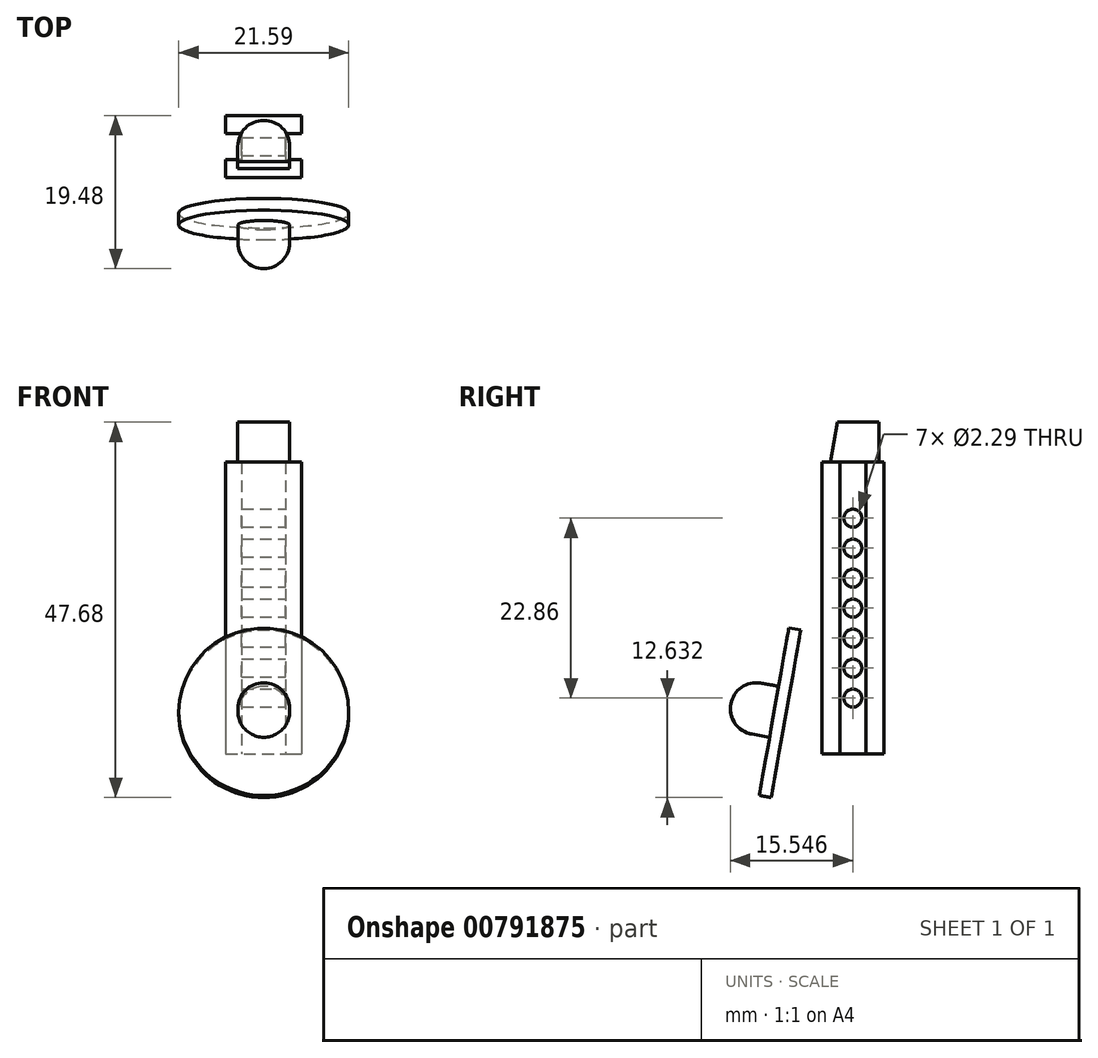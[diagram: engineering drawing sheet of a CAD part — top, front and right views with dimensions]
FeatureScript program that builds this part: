
annotation { "Feature Type Name" : "Feature", "Feature Type Description" : "" }
export const myFeature = defineFeature(function(context is Context, id is Id, definition is map)
    precondition{}
    {
        {
            var Q0;
            Q0=qCreatedBy(makeId("Top.planeOp"),FACE);
            var sketch = newSketch(context, id + "F0", { "sketchPlane" : qUnion([Q0])});
            skLineSegment(sketch, "E0.bottom", {"start": v(3.45, -0.54) * mm, "end": v(13.1, -0.54) * mm});
            skLineSegment(sketch, "E0.top", {"start": v(3.45, -8.41) * mm, "end": v(13.1, -8.41) * mm});
            skLineSegment(sketch, "E0.left", {"start": v(3.45, -0.54) * mm, "end": v(3.45, -2.82) * mm});
            skLineSegment(sketch, "E0.right", {"start": v(13.1, -0.54) * mm, "end": v(13.1, -2.82) * mm});
            skLineSegment(sketch, "E1", {"start": v(3.45, -2.82) * mm, "end": v(5.48, -2.82) * mm});
            skLineSegment(sketch, "E2", {"start": v(5.48, -2.82) * mm, "end": v(5.48, -6.12) * mm});
            skLineSegment(sketch, "E3", {"start": v(5.48, -6.12) * mm, "end": v(3.45, -6.12) * mm});
            skLineSegment(sketch, "E4.trimOffspring", {"start": v(3.45, -6.12) * mm, "end": v(3.45, -8.41) * mm});
            skLineSegment(sketch, "E5", {"start": v(13.1, -2.82) * mm, "end": v(11.07, -2.82) * mm});
            skLineSegment(sketch, "E6", {"start": v(11.07, -2.82) * mm, "end": v(11.07, -6.12) * mm});
            skLineSegment(sketch, "E7", {"start": v(11.07, -6.12) * mm, "end": v(13.1, -6.12) * mm});
            skLineSegment(sketch, "E8.trimOffspring", {"start": v(13.1, -6.12) * mm, "end": v(13.1, -8.41) * mm});
            skSolve(sketch);
        }
        {
            var Q0;
            Q0=makeQuery(id+"F0.imprint","IMPRINT",FACE,{"disambiguationData":[TD([[makeQuery(id+"F0.imprint","IMPRINT",EDGE,{"derivedFrom":sQuery(id+"F0.wireOp",EDGE,"E0.bottom")}),-1.0]])]});
            extrude(context, id + "F1", {"entities" : qUnion([Q0]), "depth" : 37.08 * mm, "offsetDistance" : 25.4 * mm});
        }
        {
            var Q0;
            Q0=makeQuery(id+"F1.opExtrude","SWEPT_FACE",FACE,{"disambiguationData":[OSD([sQuery(id+"F0.wireOp",EDGE,"E6")])]});
            var sketch = newSketch(context, id + "F2", { "sketchPlane" : qUnion([Q0])});
            skCircle(sketch, "E9", {"center": v(-4.47, 29.97) * mm, "radius": 1.14 * mm});
            skCircle(sketch, "E10", {"center": v(-4.47, 26.16) * mm, "radius": 1.14 * mm});
            skCircle(sketch, "E11", {"center": v(-4.47, 22.35) * mm, "radius": 1.14 * mm});
            skCircle(sketch, "E12", {"center": v(-4.47, 18.54) * mm, "radius": 1.14 * mm});
            skCircle(sketch, "E13", {"center": v(-4.47, 14.73) * mm, "radius": 1.14 * mm});
            skCircle(sketch, "E14", {"center": v(-4.47, 10.92) * mm, "radius": 1.14 * mm});
            skCircle(sketch, "E15", {"center": v(-4.47, 7.11) * mm, "radius": 1.14 * mm});
            skLineSegment(sketch, "E16", {"start": v(-4.47, 37.08) * mm, "end": v(-4.47, 29.97) * mm});
            skLineSegment(sketch, "E17", {"start": v(-4.47, 29.97) * mm, "end": v(-4.47, 26.16) * mm});
            skLineSegment(sketch, "E18", {"start": v(-4.47, 26.16) * mm, "end": v(-4.47, 22.35) * mm});
            skLineSegment(sketch, "E19", {"start": v(-4.47, 22.35) * mm, "end": v(-4.47, 18.54) * mm});
            skLineSegment(sketch, "E20", {"start": v(-4.47, 18.54) * mm, "end": v(-4.47, 14.73) * mm});
            skLineSegment(sketch, "E21", {"start": v(-4.47, 14.73) * mm, "end": v(-4.47, 10.92) * mm});
            skLineSegment(sketch, "E22", {"start": v(-4.47, 10.92) * mm, "end": v(-4.47, 7.11) * mm});
            skPoint(sketch, "E23", {"position": v(-4.47, 0) * mm});
            skLineSegment(sketch, "E24", {"start": v(-4.47, 7.11) * mm, "end": v(-4.47, 0) * mm});
            skSolve(sketch);
        }
        {
            var Q0;
            {var subQ0=sQuery(id+"F2.wireOp",EDGE,"E17");var subQ1=sQuery(id+"F2.wireOp",EDGE,"E9");var subQ2=makeQuery(id+"F2.imprint","INTERSECT",VERTEX,{"derivedFrom":[subQ1,subQ0]});Q0=makeQuery(id+"F2.imprint","IMPRINT",FACE,{"disambiguationData":[TD([[makeQuery(id+"F2.imprint","IMPRINT",EDGE,{"disambiguationData":[TD([[subQ2,1.0]])],"derivedFrom":subQ1}),1.0]])]});}
            var Q1;
            {var subQ0=sQuery(id+"F2.wireOp",EDGE,"E17");var subQ1=sQuery(id+"F2.wireOp",EDGE,"E9");var subQ2=makeQuery(id+"F2.imprint","INTERSECT",VERTEX,{"derivedFrom":[subQ1,subQ0]});Q1=makeQuery(id+"F2.imprint","IMPRINT",FACE,{"disambiguationData":[TD([[makeQuery(id+"F2.imprint","IMPRINT",EDGE,{"disambiguationData":[TD([[subQ2,-1.0]])],"derivedFrom":subQ1}),1.0]])]});}
            var Q2;
            {var subQ0=sQuery(id+"F2.wireOp",EDGE,"E18");var subQ1=sQuery(id+"F2.wireOp",EDGE,"E10");var subQ2=makeQuery(id+"F2.imprint","INTERSECT",VERTEX,{"derivedFrom":[subQ1,subQ0]});Q2=makeQuery(id+"F2.imprint","IMPRINT",FACE,{"disambiguationData":[TD([[makeQuery(id+"F2.imprint","IMPRINT",EDGE,{"disambiguationData":[TD([[subQ2,-1.0]])],"derivedFrom":subQ1}),1.0]])]});}
            var Q3;
            {var subQ0=sQuery(id+"F2.wireOp",EDGE,"E18");var subQ1=sQuery(id+"F2.wireOp",EDGE,"E10");var subQ2=makeQuery(id+"F2.imprint","INTERSECT",VERTEX,{"derivedFrom":[subQ1,subQ0]});Q3=makeQuery(id+"F2.imprint","IMPRINT",FACE,{"disambiguationData":[TD([[makeQuery(id+"F2.imprint","IMPRINT",EDGE,{"disambiguationData":[TD([[subQ2,1.0]])],"derivedFrom":subQ1}),1.0]])]});}
            var Q4;
            {var subQ0=sQuery(id+"F2.wireOp",EDGE,"E19");var subQ1=sQuery(id+"F2.wireOp",EDGE,"E11");var subQ2=makeQuery(id+"F2.imprint","INTERSECT",VERTEX,{"derivedFrom":[subQ1,subQ0]});Q4=makeQuery(id+"F2.imprint","IMPRINT",FACE,{"disambiguationData":[TD([[makeQuery(id+"F2.imprint","IMPRINT",EDGE,{"disambiguationData":[TD([[subQ2,1.0]])],"derivedFrom":subQ1}),1.0]])]});}
            var Q5;
            {var subQ0=sQuery(id+"F2.wireOp",EDGE,"E19");var subQ1=sQuery(id+"F2.wireOp",EDGE,"E11");var subQ2=makeQuery(id+"F2.imprint","INTERSECT",VERTEX,{"derivedFrom":[subQ1,subQ0]});Q5=makeQuery(id+"F2.imprint","IMPRINT",FACE,{"disambiguationData":[TD([[makeQuery(id+"F2.imprint","IMPRINT",EDGE,{"disambiguationData":[TD([[subQ2,-1.0]])],"derivedFrom":subQ1}),1.0]])]});}
            var Q6;
            {var subQ0=sQuery(id+"F2.wireOp",EDGE,"E20");var subQ1=sQuery(id+"F2.wireOp",EDGE,"E12");var subQ2=makeQuery(id+"F2.imprint","INTERSECT",VERTEX,{"derivedFrom":[subQ1,subQ0]});Q6=makeQuery(id+"F2.imprint","IMPRINT",FACE,{"disambiguationData":[TD([[makeQuery(id+"F2.imprint","IMPRINT",EDGE,{"disambiguationData":[TD([[subQ2,-1.0]])],"derivedFrom":subQ1}),1.0]])]});}
            var Q7;
            {var subQ0=sQuery(id+"F2.wireOp",EDGE,"E20");var subQ1=sQuery(id+"F2.wireOp",EDGE,"E12");var subQ2=makeQuery(id+"F2.imprint","INTERSECT",VERTEX,{"derivedFrom":[subQ1,subQ0]});Q7=makeQuery(id+"F2.imprint","IMPRINT",FACE,{"disambiguationData":[TD([[makeQuery(id+"F2.imprint","IMPRINT",EDGE,{"disambiguationData":[TD([[subQ2,1.0]])],"derivedFrom":subQ1}),1.0]])]});}
            var Q8;
            {var subQ0=sQuery(id+"F2.wireOp",EDGE,"E21");var subQ1=sQuery(id+"F2.wireOp",EDGE,"E13");var subQ2=makeQuery(id+"F2.imprint","INTERSECT",VERTEX,{"derivedFrom":[subQ1,subQ0]});Q8=makeQuery(id+"F2.imprint","IMPRINT",FACE,{"disambiguationData":[TD([[makeQuery(id+"F2.imprint","IMPRINT",EDGE,{"disambiguationData":[TD([[subQ2,1.0]])],"derivedFrom":subQ1}),1.0]])]});}
            var Q9;
            {var subQ0=sQuery(id+"F2.wireOp",EDGE,"E21");var subQ1=sQuery(id+"F2.wireOp",EDGE,"E13");var subQ2=makeQuery(id+"F2.imprint","INTERSECT",VERTEX,{"derivedFrom":[subQ1,subQ0]});Q9=makeQuery(id+"F2.imprint","IMPRINT",FACE,{"disambiguationData":[TD([[makeQuery(id+"F2.imprint","IMPRINT",EDGE,{"disambiguationData":[TD([[subQ2,-1.0]])],"derivedFrom":subQ1}),1.0]])]});}
            var Q10;
            {var subQ0=sQuery(id+"F2.wireOp",EDGE,"E22");var subQ1=sQuery(id+"F2.wireOp",EDGE,"E14");var subQ2=makeQuery(id+"F2.imprint","INTERSECT",VERTEX,{"derivedFrom":[subQ1,subQ0]});Q10=makeQuery(id+"F2.imprint","IMPRINT",FACE,{"disambiguationData":[TD([[makeQuery(id+"F2.imprint","IMPRINT",EDGE,{"disambiguationData":[TD([[subQ2,-1.0]])],"derivedFrom":subQ1}),1.0]])]});}
            var Q11;
            {var subQ0=sQuery(id+"F2.wireOp",EDGE,"E22");var subQ1=sQuery(id+"F2.wireOp",EDGE,"E14");var subQ2=makeQuery(id+"F2.imprint","INTERSECT",VERTEX,{"derivedFrom":[subQ1,subQ0]});Q11=makeQuery(id+"F2.imprint","IMPRINT",FACE,{"disambiguationData":[TD([[makeQuery(id+"F2.imprint","IMPRINT",EDGE,{"disambiguationData":[TD([[subQ2,1.0]])],"derivedFrom":subQ1}),1.0]])]});}
            var Q12;
            {var subQ0=sQuery(id+"F2.wireOp",EDGE,"E24");var subQ1=sQuery(id+"F2.wireOp",EDGE,"E15");var subQ2=makeQuery(id+"F2.imprint","INTERSECT",VERTEX,{"derivedFrom":[subQ1,subQ0]});Q12=makeQuery(id+"F2.imprint","IMPRINT",FACE,{"disambiguationData":[TD([[makeQuery(id+"F2.imprint","IMPRINT",EDGE,{"disambiguationData":[TD([[subQ2,1.0]])],"derivedFrom":subQ1}),1.0]])]});}
            var Q13;
            {var subQ0=sQuery(id+"F2.wireOp",EDGE,"E24");var subQ1=sQuery(id+"F2.wireOp",EDGE,"E15");var subQ2=makeQuery(id+"F2.imprint","INTERSECT",VERTEX,{"derivedFrom":[subQ1,subQ0]});Q13=makeQuery(id+"F2.imprint","IMPRINT",FACE,{"disambiguationData":[TD([[makeQuery(id+"F2.imprint","IMPRINT",EDGE,{"disambiguationData":[TD([[subQ2,-1.0]])],"derivedFrom":subQ1}),1.0]])]});}
            extrude(context, id + "F3", {"entities" : qUnion([Q0, Q1, Q2, Q3, Q4, Q5, Q6, Q7, Q8, Q9, Q10, Q11, Q12, Q13]), "operationType" : NewBodyOperationType.REMOVE, "oppositeDirection" : true, "depth" : 25.4 * mm, "offsetDistance" : 25.4 * mm});
        }
        {
            var Q0;
            Q0=makeQuery(id+"F1.opExtrude","CAP_FACE",FACE,{"disambiguationData":[OSD([sQuery(id+"F0.wireOp",EDGE,"E0.bottom"),sQuery(id+"F0.wireOp",EDGE,"E0.top"),sQuery(id+"F0.wireOp",EDGE,"E0.left"),sQuery(id+"F0.wireOp",EDGE,"E0.right"),sQuery(id+"F0.wireOp",EDGE,"E1"),sQuery(id+"F0.wireOp",EDGE,"E2"),sQuery(id+"F0.wireOp",EDGE,"E3"),sQuery(id+"F0.wireOp",EDGE,"E4.trimOffspring"),sQuery(id+"F0.wireOp",EDGE,"E5"),sQuery(id+"F0.wireOp",EDGE,"E6"),sQuery(id+"F0.wireOp",EDGE,"E7"),sQuery(id+"F0.wireOp",EDGE,"E8.trimOffspring")])],"isStart":false});
            var sketch = newSketch(context, id + "F4", { "sketchPlane" : qUnion([Q0])});
            skLineSegment(sketch, "E25.bottom", {"start": v(11.58, -1.17) * mm, "end": v(4.97, -1.17) * mm});
            skLineSegment(sketch, "E25.top", {"start": v(11.58, -7.78) * mm, "end": v(4.97, -7.78) * mm});
            skLineSegment(sketch, "E25.left", {"start": v(11.58, -1.17) * mm, "end": v(11.58, -7.78) * mm});
            skLineSegment(sketch, "E25.right", {"start": v(4.97, -1.17) * mm, "end": v(4.97, -7.78) * mm});
            skPoint(sketch, "E25.middle", {"position": v(8.28, -4.47) * mm});
            skPoint(sketch, "E25.middle.positionSnap0", {"position": v(5.48, -4.47) * mm});
            skPoint(sketch, "E25.middle.positionSnap1", {"position": v(8.28, -8.41) * mm});
            skPoint(sketch, "E25.centerSnap0", {"position": v(5.48, -4.47) * mm});
            skPoint(sketch, "E25.centerSnap1", {"position": v(8.28, -8.41) * mm});
            skSolve(sketch);
        }
        {
            var Q0;
            {var subQ8=sQuery(id+"F4.wireOp",EDGE,"E25.bottom");Q0=makeQuery(id+"F4.imprint","IMPRINT",FACE,{"disambiguationData":[TD([[makeQuery(id+"F4.imprint","IMPRINT",EDGE,{"derivedFrom":subQ8}),1.0]])]});}
            var Q1;
            {var subQ5=makeQuery(id+"F1.opExtrude","CAP_EDGE",EDGE,{"disambiguationData":[OSD([sQuery(id+"F0.wireOp",EDGE,"E2")])],"isStart":false});Q1=makeQuery(id+"F4.imprint","IMPRINT",FACE,{"disambiguationData":[TD([[makeQuery(id+"F4.imprint","IMPRINT",EDGE,{"derivedFrom":subQ5}),-1.0]])]});}
            var Q2;
            {var subQ5=makeQuery(id+"F1.opExtrude","CAP_EDGE",EDGE,{"disambiguationData":[OSD([sQuery(id+"F0.wireOp",EDGE,"E6")])],"isStart":false});Q2=makeQuery(id+"F4.imprint","IMPRINT",FACE,{"disambiguationData":[TD([[makeQuery(id+"F4.imprint","IMPRINT",EDGE,{"derivedFrom":subQ5}),1.0]])]});}
            extrude(context, id + "F5", {"entities" : qUnion([Q0, Q1, Q2]), "operationType" : NewBodyOperationType.ADD, "depth" : 5.08 * mm, "offsetDistance" : 25.4 * mm});
        }
        {
            var Q0;
            Q0=makeQuery(id+"F5.opExtrude","CAP_EDGE",EDGE,{"disambiguationData":[OSD([sQuery(id+"F4.wireOp",EDGE,"E25.top")])],"isStart":false});
            chamfer(context, id + "F6", {"entities" : qUnion([Q0]), "chamferType" : ChamferType.OFFSET_ANGLE, "width" : 7.62 * mm, "oppositeDirection" : true, "angle" : 10 * degree, "tangentPropagation" : true});
        }
        {
            var Q0;
            Q0=makeQuery(id+"F5.opExtrude","SWEPT_EDGE",EDGE,{"disambiguationData":[OSD([sQuery(id+"F4.wireOp",EDGE,"E25.bottom"),sQuery(id+"F4.wireOp",EDGE,"E25.right")])]});
            var Q1;
            Q1=makeQuery(id+"F5.opExtrude","SWEPT_EDGE",EDGE,{"disambiguationData":[OSD([sQuery(id+"F4.wireOp",EDGE,"E25.top"),sQuery(id+"F4.wireOp",EDGE,"E25.left")])]});
            var Q2;
            Q2=makeQuery(id+"F5.opExtrude","SWEPT_EDGE",EDGE,{"disambiguationData":[OSD([sQuery(id+"F4.wireOp",EDGE,"E25.top"),sQuery(id+"F4.wireOp",EDGE,"E25.right")])]});
            var Q3;
            Q3=makeQuery(id+"F5.opExtrude","SWEPT_EDGE",EDGE,{"disambiguationData":[OSD([sQuery(id+"F4.wireOp",EDGE,"E25.bottom"),sQuery(id+"F4.wireOp",EDGE,"E25.left")])]});
            fillet(context, id + "F7", {"entities" : qUnion([Q0, Q1, Q2, Q3]), "tangentPropagation" : true, "radius" : 3.3 * mm, "defaultsChanged" : true, "vertexSettings" : [], "allowEdgeOverflow" : false});
        }
        {
            var Q0;
            Q0=makeQuery(id+"F6.opChamfer","BLEND_FACE",FACE,{"disambiguationData":[OSD([sQuery(id+"F4.wireOp",EDGE,"E25.top")])]});
            var sketch = newSketch(context, id + "F8", { "sketchPlane" : qUnion([Q0])});
            skCircle(sketch, "E26", {"center": v(8.28, 2.78) * mm, "radius": 10.8 * mm});
            skLineSegment(sketch, "E27.bottom", {"start": v(11.57, 6.07) * mm, "end": v(4.99, 6.07) * mm});
            skLineSegment(sketch, "E27.top", {"start": v(11.57, -0.5) * mm, "end": v(4.99, -0.5) * mm});
            skLineSegment(sketch, "E27.left", {"start": v(11.57, 6.07) * mm, "end": v(11.57, -0.5) * mm});
            skLineSegment(sketch, "E27.right", {"start": v(4.99, 6.07) * mm, "end": v(4.99, -0.5) * mm});
            skSolve(sketch);
        }
        {
            var Q0;
            {var subQ0=sQuery(id+"F8.wireOp",EDGE,"ilMOxncB-kWTl-2Vke-N7D0-Fq7CKy7CLvWp");var subQ1=makeQuery(id+"F7.opFillet","BLEND_EDGE",EDGE,{"blendedFrom":[makeQuery(id+"F5.opExtrude","SWEPT_EDGE",EDGE,{"disambiguationData":[OSD([sQuery(id+"F4.wireOp",EDGE,"E25.bottom"),sQuery(id+"F4.wireOp",EDGE,"E25.left")])]}),makeQuery(id+"F6.opChamfer","BLEND_FACE",FACE,{"disambiguationData":[OSD([sQuery(id+"F4.wireOp",EDGE,"E25.top")])]})],"blendedInto":[makeQuery(id+"F6.opChamfer","BLEND_FACE",FACE,{"disambiguationData":[OSD([sQuery(id+"F4.wireOp",EDGE,"E25.top")])]})]});var subQ2=makeQuery(id+"F8.imprint","INTERSECT",VERTEX,{"disambiguationData":[OD(0.0)],"derivedFrom":[subQ1,subQ0]});Q0=makeQuery(id+"F8.imprint","IMPRINT",FACE,{"disambiguationData":[TD([[makeQuery(id+"F8.imprint","IMPRINT",EDGE,{"disambiguationData":[TD([[subQ2,-1.0]])],"derivedFrom":subQ0}),1.0]])]});}
            var Q1;
            {var subQ0=sQuery(id+"F8.wireOp",EDGE,"E27.right");var subQ1=sQuery(id+"F8.wireOp",EDGE,"E27.bottom");var subQ2=makeQuery(id+"F8.imprint","INTERSECT",VERTEX,{"derivedFrom":[subQ1,subQ0]});Q1=makeQuery(id+"F8.imprint","IMPRINT",FACE,{"disambiguationData":[TD([[makeQuery(id+"F8.imprint","IMPRINT",EDGE,{"disambiguationData":[TD([[subQ2,1.0]])],"derivedFrom":subQ1}),1.0]])]});}
            var Q2;
            {var subQ0=sQuery(id+"F8.wireOp",EDGE,"E27.left");var subQ1=sQuery(id+"F8.wireOp",EDGE,"E27.bottom");var subQ2=makeQuery(id+"F8.imprint","INTERSECT",VERTEX,{"derivedFrom":[subQ1,subQ0]});Q2=makeQuery(id+"F8.imprint","IMPRINT",FACE,{"disambiguationData":[TD([[makeQuery(id+"F8.imprint","IMPRINT",EDGE,{"disambiguationData":[TD([[subQ2,-1.0]])],"derivedFrom":subQ1}),1.0]])]});}
            var Q3;
            {var subQ0=sQuery(id+"F8.wireOp",EDGE,"E27.left");var subQ1=sQuery(id+"F8.wireOp",EDGE,"E27.top");var subQ2=makeQuery(id+"F8.imprint","INTERSECT",VERTEX,{"derivedFrom":[subQ1,subQ0]});Q3=makeQuery(id+"F8.imprint","IMPRINT",FACE,{"disambiguationData":[TD([[makeQuery(id+"F8.imprint","IMPRINT",EDGE,{"disambiguationData":[TD([[subQ2,-1.0]])],"derivedFrom":subQ1}),-1.0]])]});}
            var Q4;
            {var subQ0=sQuery(id+"F8.wireOp",EDGE,"E27.right");var subQ1=sQuery(id+"F8.wireOp",EDGE,"E27.top");var subQ2=makeQuery(id+"F8.imprint","INTERSECT",VERTEX,{"derivedFrom":[subQ1,subQ0]});Q4=makeQuery(id+"F8.imprint","IMPRINT",FACE,{"disambiguationData":[TD([[makeQuery(id+"F8.imprint","IMPRINT",EDGE,{"disambiguationData":[TD([[subQ2,1.0]])],"derivedFrom":subQ1}),-1.0]])]});}
            var Q5;
            {var subQ0=sQuery(id+"F8.wireOp",EDGE,"E27.bottom");var subQ1=makeQuery(id+"F7.opFillet","BLEND_EDGE",EDGE,{"blendedFrom":[makeQuery(id+"F5.opExtrude","SWEPT_EDGE",EDGE,{"disambiguationData":[OSD([sQuery(id+"F4.wireOp",EDGE,"E25.bottom"),sQuery(id+"F4.wireOp",EDGE,"E25.left")])]}),makeQuery(id+"F6.opChamfer","BLEND_FACE",FACE,{"disambiguationData":[OSD([sQuery(id+"F4.wireOp",EDGE,"E25.top")])]})],"blendedInto":[makeQuery(id+"F6.opChamfer","BLEND_FACE",FACE,{"disambiguationData":[OSD([sQuery(id+"F4.wireOp",EDGE,"E25.top")])]})]});var subQ4=makeQuery(id+"F8.imprint","INTERSECT",VERTEX,{"disambiguationData":[OD(0.0)],"derivedFrom":[subQ1,subQ0]});Q5=makeQuery(id+"F8.imprint","IMPRINT",FACE,{"disambiguationData":[TD([[makeQuery(id+"F8.imprint","IMPRINT",EDGE,{"disambiguationData":[TD([[subQ4,-1.0]])],"derivedFrom":subQ0}),1.0]])]});}
            extrude(context, id + "F9", {"entities" : qUnion([Q0, Q1, Q2, Q3, Q4, Q5]), "operationType" : NewBodyOperationType.ADD, "depth" : 7.11 * mm, "offsetDistance" : 25.4 * mm});
        }
        {
            var Q0;
            Q0=makeQuery(id+"F8.imprint","IMPRINT",FACE,{"disambiguationData":[TD([[makeQuery(id+"F8.imprint","IMPRINT",EDGE,{"derivedFrom":sQuery(id+"F8.wireOp",EDGE,"E26")}),1.0]])]});
            extrude(context, id + "F10", {"entities" : qUnion([Q0]), "depth" : 1.52 * mm, "offsetDistance" : 25.4 * mm});
        }
        {
            var Q0;
            Q0=makeQuery(id+"F9.opExtrude","SWEPT_FACE",FACE,{"disambiguationData":[OSD([sQuery(id+"F8.wireOp",EDGE,"E27.left")])]});
            var sketch = newSketch(context, id + "F11", { "sketchPlane" : qUnion([Q0])});
            skCircle(sketch, "E28", {"center": v(-5.63, 45.8) * mm, "radius": 0.89 * mm});
            skSolve(sketch);
        }
        {
            var Q0;
            Q0=makeQuery(id+"F11.imprint","IMPRINT",FACE,{"disambiguationData":[TD([[makeQuery(id+"F11.imprint","IMPRINT",EDGE,{"derivedFrom":sQuery(id+"F11.wireOp",EDGE,"E28")}),1.0]])]});
            extrude(context, id + "F12", {"entities" : qUnion([Q0]), "operationType" : NewBodyOperationType.REMOVE, "oppositeDirection" : true, "depth" : 25.4 * mm, "offsetDistance" : 25.4 * mm});
        }
        {
            var Q0;
            Q0=makeQuery(id+"F9.opExtrude","SWEPT_EDGE",EDGE,{"disambiguationData":[OSD([sQuery(id+"F8.wireOp",EDGE,"E27.top"),sQuery(id+"F8.wireOp",EDGE,"E27.left")])]});
            var Q1;
            Q1=makeQuery(id+"F9.opExtrude","SWEPT_EDGE",EDGE,{"disambiguationData":[OSD([sQuery(id+"F8.wireOp",EDGE,"E27.top"),sQuery(id+"F8.wireOp",EDGE,"E27.right")])]});
            var Q2;
            Q2=makeQuery(id+"F9.opExtrude","SWEPT_EDGE",EDGE,{"disambiguationData":[OSD([sQuery(id+"F8.wireOp",EDGE,"E27.bottom"),sQuery(id+"F8.wireOp",EDGE,"E27.left")])]});
            var Q3;
            Q3=makeQuery(id+"F9.opExtrude","SWEPT_EDGE",EDGE,{"disambiguationData":[OSD([sQuery(id+"F8.wireOp",EDGE,"E27.bottom"),sQuery(id+"F8.wireOp",EDGE,"E27.right")])]});
            fillet(context, id + "F13", {"entities" : qUnion([Q0, Q1, Q2, Q3]), "tangentPropagation" : true, "radius" : 3.3 * mm, "defaultsChanged" : true, "vertexSettings" : [], "allowEdgeOverflow" : false});
        }
        {
            var Q0;
            {var subQ0=sQuery(id+"F8.wireOp",EDGE,"E27.left");var subQ1=sQuery(id+"F8.wireOp",EDGE,"E27.bottom");var subQ2=makeQuery(id+"F8.imprint","INTERSECT",VERTEX,{"derivedFrom":[subQ1,subQ0]});Q0=makeQuery(id+"F8.imprint","IMPRINT",FACE,{"disambiguationData":[TD([[makeQuery(id+"F8.imprint","IMPRINT",EDGE,{"disambiguationData":[TD([[subQ2,-1.0]])],"derivedFrom":subQ1}),1.0]])]});}
            var Q1;
            {var subQ0=sQuery(id+"F8.wireOp",EDGE,"E27.right");var subQ1=sQuery(id+"F8.wireOp",EDGE,"E27.bottom");var subQ2=makeQuery(id+"F8.imprint","INTERSECT",VERTEX,{"derivedFrom":[subQ1,subQ0]});Q1=makeQuery(id+"F8.imprint","IMPRINT",FACE,{"disambiguationData":[TD([[makeQuery(id+"F8.imprint","IMPRINT",EDGE,{"disambiguationData":[TD([[subQ2,1.0]])],"derivedFrom":subQ1}),1.0]])]});}
            var Q2;
            {var subQ0=sQuery(id+"F8.wireOp",EDGE,"E27.right");var subQ1=sQuery(id+"F8.wireOp",EDGE,"E27.top");var subQ2=makeQuery(id+"F8.imprint","INTERSECT",VERTEX,{"derivedFrom":[subQ1,subQ0]});Q2=makeQuery(id+"F8.imprint","IMPRINT",FACE,{"disambiguationData":[TD([[makeQuery(id+"F8.imprint","IMPRINT",EDGE,{"disambiguationData":[TD([[subQ2,1.0]])],"derivedFrom":subQ1}),-1.0]])]});}
            var Q3;
            {var subQ0=sQuery(id+"F8.wireOp",EDGE,"E27.left");var subQ1=sQuery(id+"F8.wireOp",EDGE,"E27.top");var subQ2=makeQuery(id+"F8.imprint","INTERSECT",VERTEX,{"derivedFrom":[subQ1,subQ0]});Q3=makeQuery(id+"F8.imprint","IMPRINT",FACE,{"disambiguationData":[TD([[makeQuery(id+"F8.imprint","IMPRINT",EDGE,{"disambiguationData":[TD([[subQ2,-1.0]])],"derivedFrom":subQ1}),-1.0]])]});}
            extrude(context, id + "F14", {"entities" : qUnion([Q0, Q1, Q2, Q3]), "operationType" : NewBodyOperationType.ADD, "depth" : 1.52 * mm, "offsetDistance" : 25.4 * mm});
        }
        {
            var Q0;
            {var subQ0=sQuery(id+"F8.wireOp",EDGE,"E27.left");var subQ1=sQuery(id+"F8.wireOp",EDGE,"E27.bottom");Q0=makeQuery(id+"F13.opFillet","BLEND_EDGE",EDGE,{"blendedFrom":[makeQuery(id+"F9.opExtrude","SWEPT_EDGE",EDGE,{"disambiguationData":[OSD([subQ1,subQ0])]}),makeQuery(id+"F9.opExtrude","CAP_FACE",FACE,{"disambiguationData":[OSD([subQ1,sQuery(id+"F8.wireOp",EDGE,"E27.top"),subQ0,sQuery(id+"F8.wireOp",EDGE,"E27.right")])],"isStart":false})],"blendedInto":[makeQuery(id+"F9.opExtrude","CAP_FACE",FACE,{"disambiguationData":[OSD([subQ1,sQuery(id+"F8.wireOp",EDGE,"E27.top"),subQ0,sQuery(id+"F8.wireOp",EDGE,"E27.right")])],"isStart":false})]});}
            fillet(context, id + "F15", {"entities" : qUnion([Q0]), "tangentPropagation" : true, "radius" : 3.3 * mm, "defaultsChanged" : true, "vertexSettings" : [], "allowEdgeOverflow" : false});
        }
    });
